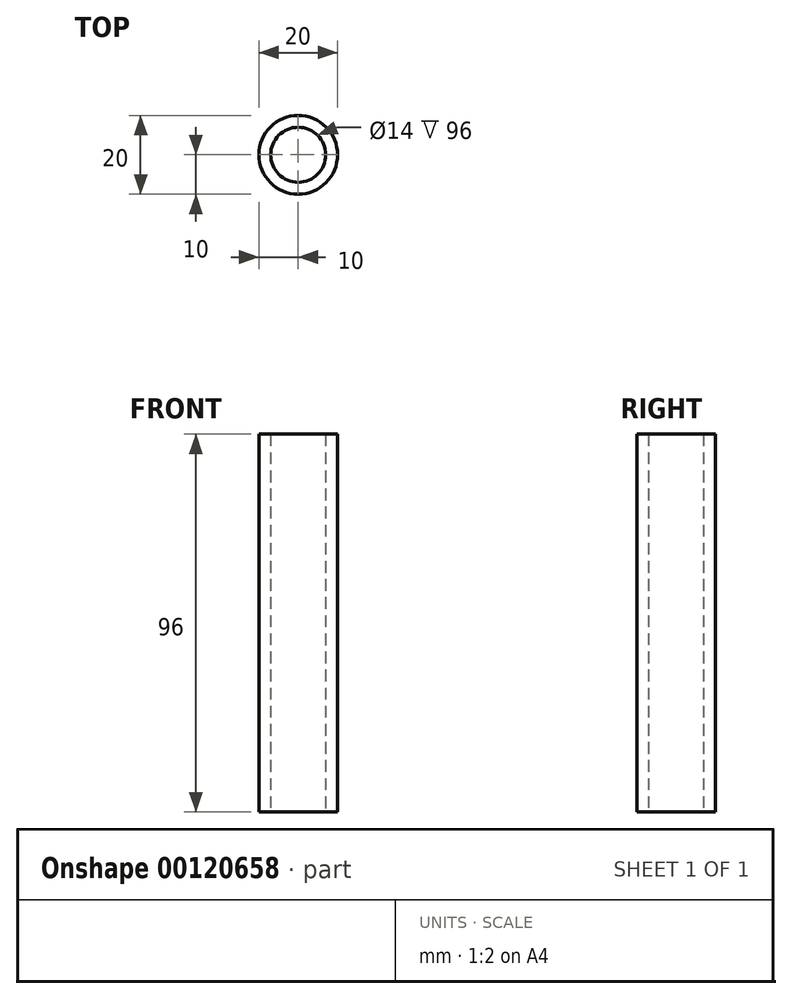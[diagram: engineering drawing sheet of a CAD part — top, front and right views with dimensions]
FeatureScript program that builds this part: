
annotation { "Feature Type Name" : "Feature", "Feature Type Description" : "" }
export const myFeature = defineFeature(function(context is Context, id is Id, definition is map)
    precondition{}
    {
        {
            var Q0;
            Q0=qCreatedBy(makeId("Top.planeOp"),FACE);
            var sketch = newSketch(context, id + "F0", { "sketchPlane" : qUnion([Q0])});
            skCircle(sketch, "E0", {"center": v(0, 0) * mm, "radius": 10 * mm});
            skCircle(sketch, "E1", {"center": v(0, 0) * mm, "radius": 7 * mm});
            skSolve(sketch);
        }
        {
            var Q0;
            Q0=makeQuery(id+"F0.imprint","IMPRINT",FACE,{"disambiguationData":[TD([[makeQuery(id+"F0.imprint","IMPRINT",EDGE,{"derivedFrom":sQuery(id+"F0.wireOp",EDGE,"E0")}),1.0]])]});
            extrude(context, id + "F1", {"entities" : qUnion([Q0]), "depth" : 96 * mm});
        }
    });
